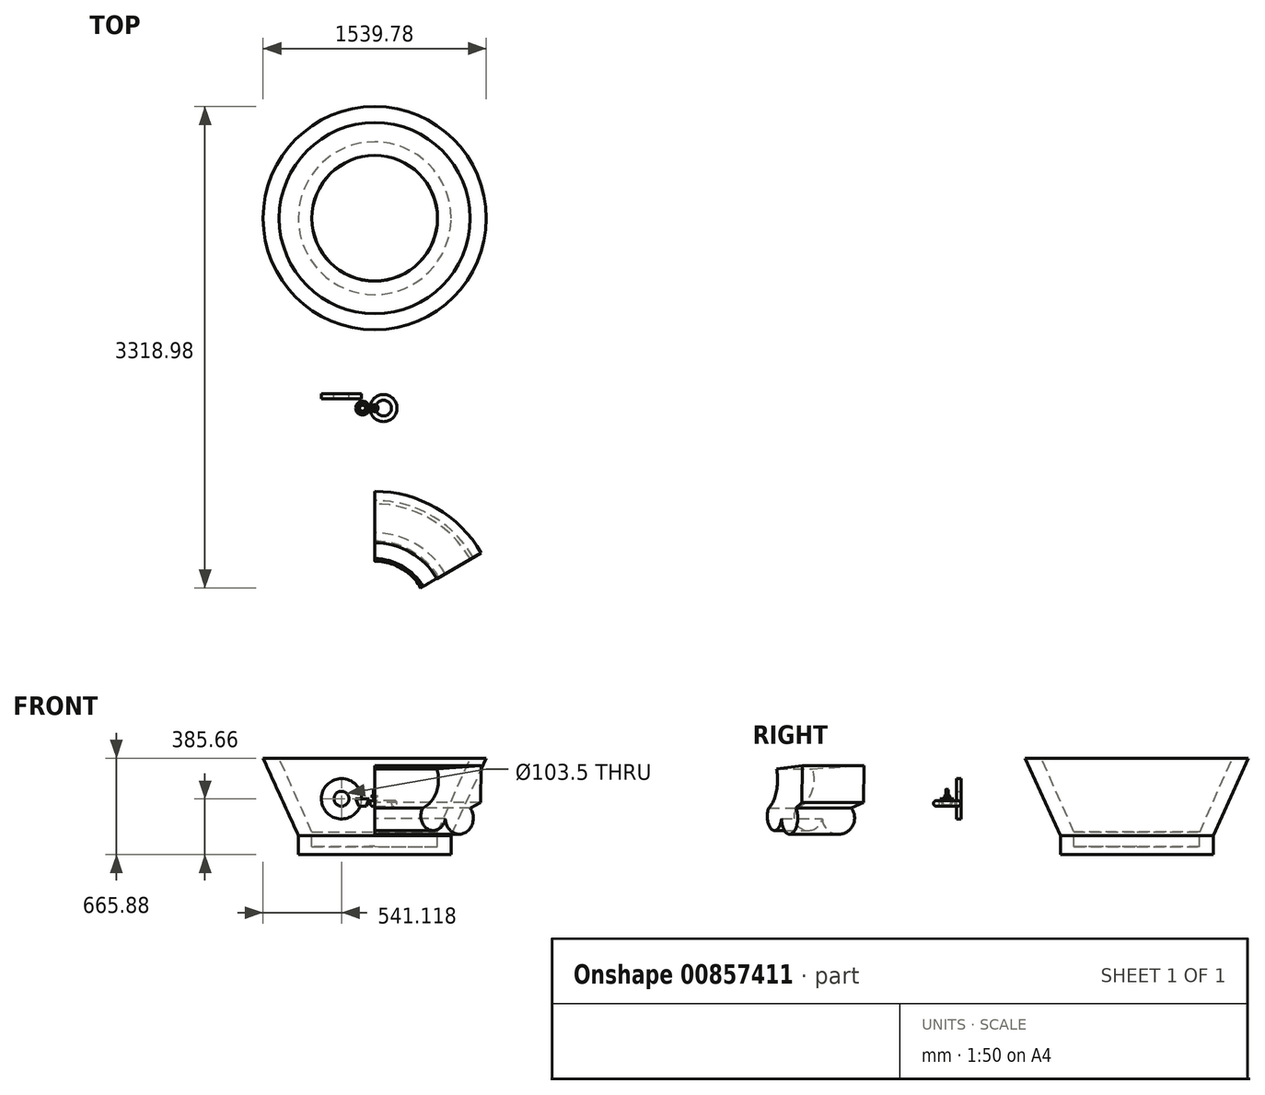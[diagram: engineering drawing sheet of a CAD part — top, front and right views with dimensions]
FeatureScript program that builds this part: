
annotation { "Feature Type Name" : "Feature", "Feature Type Description" : "" }
export const myFeature = defineFeature(function(context is Context, id is Id, definition is map)
    precondition{}
    {
        {
            var Q0;
            Q0=qCreatedBy(makeId("Front.planeOp"),FACE);
            var sketch = newSketch(context, id + "F0", { "sketchPlane" : qUnion([Q0])});
            skLineSegment(sketch, "E0", {"start": v(0, 65.1) * mm, "end": v(0, 0) * mm});
            skLineSegment(sketch, "E1", {"start": v(0, 0) * mm, "end": v(-23.77, 19.34) * mm});
            skLineSegment(sketch, "E2", {"start": v(-23.77, 19.34) * mm, "end": v(-7.82, 19.34) * mm});
            skLineSegment(sketch, "E3", {"start": v(-7.82, 19.34) * mm, "end": v(-7.82, 64.5) * mm});
            skLineSegment(sketch, "E4", {"start": v(-7.82, 64.5) * mm, "end": v(0, 65.1) * mm});
            skSolve(sketch);
        }
        {
            var Q0;
            Q0=makeQuery(id+"F0.imprint","IMPRINT",FACE,{"disambiguationData":[TD([[makeQuery(id+"F0.imprint","IMPRINT",EDGE,{"derivedFrom":sQuery(id+"F0.wireOp",EDGE,"E0")}),-1.0]])]});
            var Q1;
            Q1=sQuery(id+"F0.wireOp",EDGE,"E0");
            revolve(context, id + "F1", {"surfaceOperationType" : NewSurfaceOperationType.NEW, "entities" : qUnion([Q0]), "axis" : qUnion([Q1]), "revolveType" : RevolveType.FULL});
        }
        {
            var Q0;
            Q0=qCreatedBy(makeId("Front.planeOp"),FACE);
            var sketch = newSketch(context, id + "F2", { "sketchPlane" : qUnion([Q0])});
            skLineSegment(sketch, "E5", {"start": v(-131.23, 0) * mm, "end": v(-110.86, -50.04) * mm});
            skLineSegment(sketch, "E6", {"start": v(-110.86, -50.04) * mm, "end": v(-83.7, -50.04) * mm});
            skLineSegment(sketch, "E7", {"start": v(-83.7, -50.04) * mm, "end": v(-83.7, 0) * mm});
            skLineSegment(sketch, "E8", {"start": v(-83.7, 0) * mm, "end": v(-131.23, 0) * mm});
            skLineSegment(sketch, "E9", {"start": v(-121.85, 0) * mm, "end": v(-103.9, -44.1) * mm});
            skLineSegment(sketch, "E10", {"start": v(-103.9, -44.1) * mm, "end": v(-83.7, -44.1) * mm});
            skSolve(sketch);
        }
        {
            var Q0;
            Q0=makeQuery(id+"F2.imprint","IMPRINT",FACE,{"disambiguationData":[TD([[makeQuery(id+"F2.imprint","IMPRINT",EDGE,{"derivedFrom":sQuery(id+"F2.wireOp",EDGE,"E5")}),1.0]])]});
            var sketch = newSketch(context, id + "F3", { "sketchPlane" : qUnion([Q0])});
            skSolve(sketch);
        }
        {
            var Q0;
            {var subQ1=sQuery(id+"F2.wireOp",EDGE,"E5");Q0=makeQuery(id+"F3.imprint","IMPRINT",FACE,{"disambiguationData":[TD([[makeQuery(id+"F3.imprint","IMPRINT",EDGE,{"derivedFrom":makeQuery(id+"F2.imprint","IMPRINT",EDGE,{"derivedFrom":subQ1})}),1.0]])]});}
            var Q1;
            Q1=sQuery(id+"F2.wireOp",EDGE,"E7");
            revolve(context, id + "F4", {"surfaceOperationType" : NewSurfaceOperationType.NEW, "entities" : qUnion([Q0]), "axis" : qUnion([Q1]), "revolveType" : RevolveType.FULL});
        }
        {
            var Q0;
            Q0=qCreatedBy(makeId("Front.planeOp"),FACE);
            var sketch = newSketch(context, id + "F5", { "sketchPlane" : qUnion([Q0])});
            skCircle(sketch, "E11", {"center": v(-12.6, -32.03) * mm, "radius": 19.32 * mm});
            skLineSegment(sketch, "E12", {"start": v(61.2, -13.14) * mm, "end": v(61.2, -55.06) * mm});
            skSolve(sketch);
        }
        {
            var Q0;
            Q0 = qSketchRegion(id + "F5", true);
            var Q1;
            Q1=sQuery(id+"F5.wireOp",EDGE,"E12");
            revolve(context, id + "F6", {"surfaceOperationType" : NewSurfaceOperationType.NEW, "entities" : qUnion([Q0]), "axis" : qUnion([Q1]), "revolveType" : RevolveType.FULL});
        }
        {
            var Q0;
            Q0=qCreatedBy(makeId("Top.planeOp"),FACE);
            var sketch = newSketch(context, id + "F7", { "sketchPlane" : qUnion([Q0])});
            skLineSegment(sketch, "E13.bottom", {"start": v(-367.57, 97.93) * mm, "end": v(-280.52, 97.93) * mm});
            skLineSegment(sketch, "E13.top", {"start": v(-367.57, 64.17) * mm, "end": v(-280.52, 64.17) * mm});
            skLineSegment(sketch, "E13.left", {"start": v(-367.57, 97.93) * mm, "end": v(-367.57, 64.17) * mm});
            skLineSegment(sketch, "E13.right", {"start": v(-280.52, 97.93) * mm, "end": v(-280.52, 64.17) * mm});
            skLineSegment(sketch, "E14", {"start": v(-228.77, 107.11) * mm, "end": v(-228.77, 22.91) * mm});
            skSolve(sketch);
        }
        {
            var Q0;
            Q0 = qSketchRegion(id + "F7", true);
            var Q1;
            Q1=sQuery(id+"F7.wireOp",EDGE,"E14");
            revolve(context, id + "F8", {"operationType" : NewBodyOperationType.ADD, "surfaceOperationType" : NewSurfaceOperationType.NEW, "entities" : qUnion([Q0]), "axis" : qUnion([Q1]), "revolveType" : RevolveType.FULL});
        }
        {
            var Q0;
            Q0=qCreatedBy(makeId("Right.planeOp"),FACE);
            var sketch = newSketch(context, id + "F9", { "sketchPlane" : qUnion([Q0])});
            skLineSegment(sketch, "E15", {"start": v(-574.14, 228.05) * mm, "end": v(-577.3, -25.82) * mm});
            skLineSegment(sketch, "E16", {"start": v(-577.3, -25.82) * mm, "end": v(-660.95, -64.37) * mm});
            skArc(sketch, "E17", {"start": v(-860.22, -135.86) * mm, "mid": v(-711.14, -237.93) * mm, "end": v(-660.95, -64.37) * mm});
            skArc(sketch, "E18", {"start": v(-1038.18, -64.37) * mm, "mid": v(-993.98, -211.6) * mm, "end": v(-860.22, -135.86) * mm});
            skArc(sketch, "E19", {"start": v(-1038.18, -64.37) * mm, "mid": v(-930.21, 49.8) * mm, "end": v(-928.67, 206.93) * mm});
            skLineSegment(sketch, "E20", {"start": v(-928.67, 206.93) * mm, "end": v(-574.14, 228.05) * mm});
            skLineSegment(sketch, "E21", {"start": v(-1423.02, 153.14) * mm, "end": v(-1423.02, -201.27) * mm});
            skSolve(sketch);
        }
        {
            var Q0;
            Q0=makeQuery(id+"F9.imprint","IMPRINT",FACE,{"disambiguationData":[TD([[makeQuery(id+"F9.imprint","IMPRINT",EDGE,{"derivedFrom":sQuery(id+"F9.wireOp",EDGE,"E15")}),-1.0]])]});
            var Q1;
            Q1=sQuery(id+"F9.wireOp",EDGE,"E21");
            revolve(context, id + "F10", {"surfaceOperationType" : NewSurfaceOperationType.NEW, "entities" : qUnion([Q0]), "axis" : qUnion([Q1]), "revolveType" : RevolveType.ONE_DIRECTION, "angle" : 60 * degree});
        }
        {
            var Q0;
            Q0=makeQuery(id+"F10.opRevolve","CAP_FACE",FACE,{"disambiguationData":[OSD([sQuery(id+"F9.wireOp",EDGE,"E15"),sQuery(id+"F9.wireOp",EDGE,"E16"),sQuery(id+"F9.wireOp",EDGE,"E17"),sQuery(id+"F9.wireOp",EDGE,"E18"),sQuery(id+"F9.wireOp",EDGE,"E19"),sQuery(id+"F9.wireOp",EDGE,"E20")])],"isStart":true});
            var sketch = newSketch(context, id + "F11", { "sketchPlane" : qUnion([Q0])});
            skLineSegment(sketch, "E22", {"start": v(-2079.64, 279.47) * mm, "end": v(-1836.6, -253.23) * mm});
            skLineSegment(sketch, "E23", {"start": v(-1836.6, -253.23) * mm, "end": v(-1836.6, -385.66) * mm});
            skLineSegment(sketch, "E24", {"start": v(-1836.6, -385.66) * mm, "end": v(-1309.75, -385.66) * mm});
            skLineSegment(sketch, "E25", {"start": v(-1309.75, -385.66) * mm, "end": v(-1309.75, 284.62) * mm});
            skLineSegment(sketch, "E26", {"start": v(-1309.75, 284.62) * mm, "end": v(-2079.64, 279.47) * mm});
            skLineSegment(sketch, "E27", {"start": v(-1968.8, 280.22) * mm, "end": v(-1743.52, -229.27) * mm});
            skLineSegment(sketch, "E28", {"start": v(-1743.52, -229.27) * mm, "end": v(-1742.84, -331.4) * mm});
            skLineSegment(sketch, "E29", {"start": v(-1742.84, -331.4) * mm, "end": v(-1309.75, -328.51) * mm});
            skSolve(sketch);
        }
        {
            var Q0;
            {var subQ3=sQuery(id+"F11.wireOp",EDGE,"E22");Q0=makeQuery(id+"F11.imprint","IMPRINT",FACE,{"disambiguationData":[TD([[makeQuery(id+"F11.imprint","IMPRINT",EDGE,{"derivedFrom":subQ3}),1.0]])]});}
            var Q1;
            Q1=sQuery(id+"F11.wireOp",EDGE,"E25");
            revolve(context, id + "F12", {"surfaceOperationType" : NewSurfaceOperationType.NEW, "entities" : qUnion([Q0]), "axis" : qUnion([Q1]), "revolveType" : RevolveType.FULL});
        }
    });
